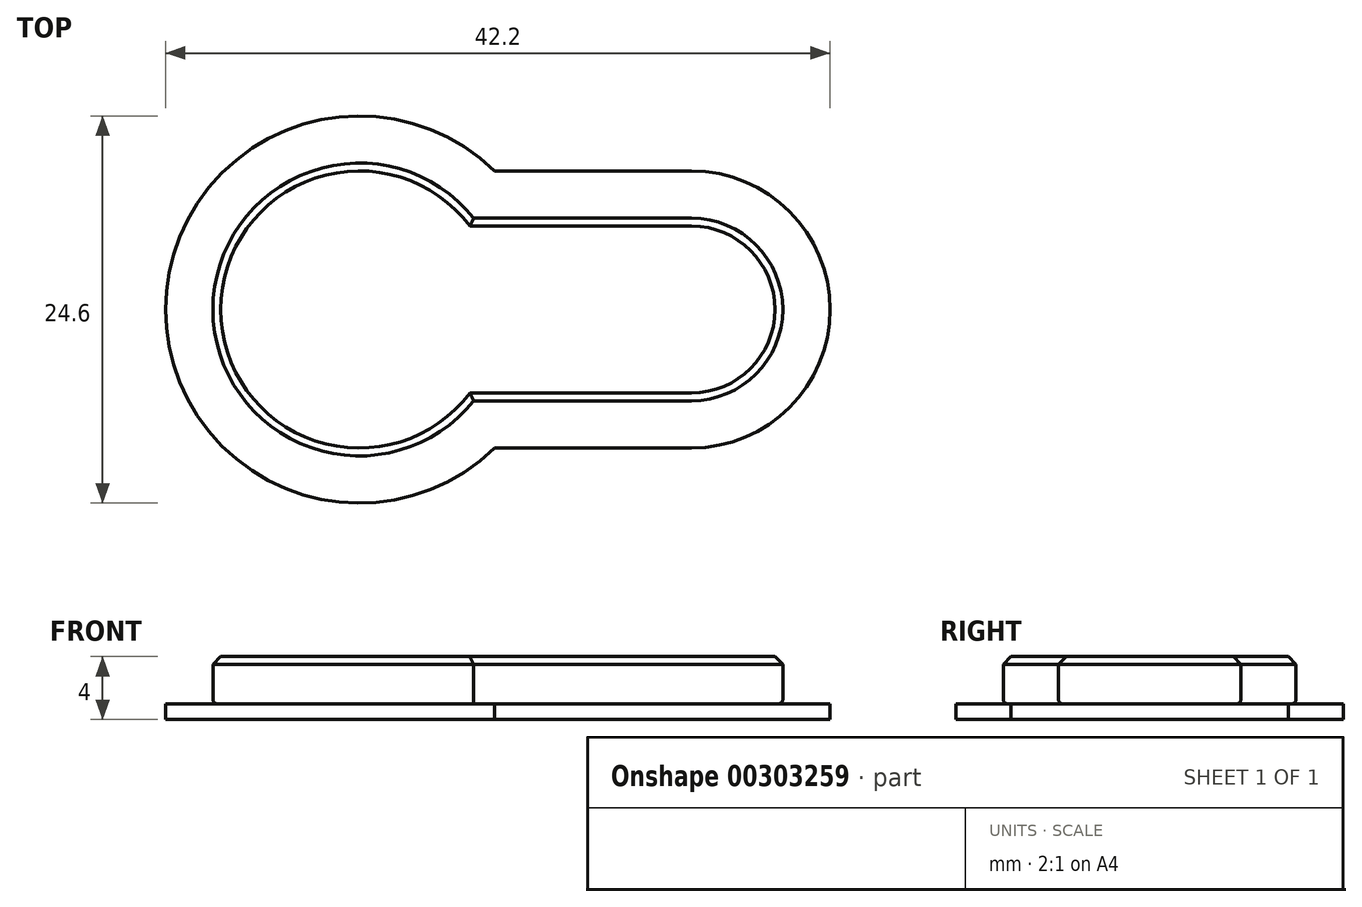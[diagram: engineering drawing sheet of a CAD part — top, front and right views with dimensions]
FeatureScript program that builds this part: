
annotation { "Feature Type Name" : "Feature", "Feature Type Description" : "" }
export const myFeature = defineFeature(function(context is Context, id is Id, definition is map)
    precondition{}
    {
        {
            var Q0;
            Q0=qCreatedBy(makeId("Top.planeOp"),FACE);
            var sketch = newSketch(context, id + "F0", { "sketchPlane" : qUnion([Q0])});
            skArc(sketch, "E0", {"start": v(7.27, 5.8) * mm, "mid": v(-9.3, 0) * mm, "end": v(7.27, -5.8) * mm});
            skArc(sketch, "E1", {"start": v(21.1, -5.8) * mm, "mid": v(26.9, 0) * mm, "end": v(21.1, 5.8) * mm});
            skLineSegment(sketch, "E2", {"start": v(-9.3, 0) * mm, "end": v(-9.3, 19.5) * mm, "construction": true});
            skLineSegment(sketch, "E3", {"start": v(26.9, 0) * mm, "end": v(26.9, 18.68) * mm, "construction": true});
            skLineSegment(sketch, "E4", {"start": v(21.1, -5.8) * mm, "end": v(21.1, 5.8) * mm, "construction": true});
            skLineSegment(sketch, "E5", {"start": v(21.1, 5.8) * mm, "end": v(7.27, 5.8) * mm});
            skLineSegment(sketch, "E6", {"start": v(21.1, -5.8) * mm, "end": v(7.27, -5.8) * mm});
            skSolve(sketch);
        }
        {
            var Q0;
            Q0 = qSketchRegion(id + "F0", true);
            extrude(context, id + "F1", {"entities" : qUnion([Q0]), "depth" : 3 * mm});
        }
        {
            var Q0;
            Q0=makeQuery(id+"F1.opExtrude","CAP_FACE",FACE,{"disambiguationData":[OSD([sQuery(id+"F0.wireOp",EDGE,"E0"),sQuery(id+"F0.wireOp",EDGE,"E1"),sQuery(id+"F0.wireOp",EDGE,"E5"),sQuery(id+"F0.wireOp",EDGE,"E6")])],"isStart":true});
            var sketch = newSketch(context, id + "F2", { "sketchPlane" : qUnion([Q0])});
            skLineSegment(sketch, "E7.0", {"start": v(21.1, -5.8) * mm, "end": v(7.27, -5.8) * mm, "construction": true});
            skArc(sketch, "E7.1", {"start": v(7.27, -5.8) * mm, "mid": v(-9.3, 0) * mm, "end": v(7.27, 5.8) * mm, "construction": true});
            skLineSegment(sketch, "E7.2", {"start": v(21.1, 5.8) * mm, "end": v(7.27, 5.8) * mm, "construction": true});
            skArc(sketch, "E7.3", {"start": v(21.1, 5.8) * mm, "mid": v(26.9, 0) * mm, "end": v(21.1, -5.8) * mm, "construction": true});
            skArc(sketch, "E8.0", {"start": v(21.1, 8.8) * mm, "mid": v(29.9, 0) * mm, "end": v(21.1, -8.8) * mm});
            skLineSegment(sketch, "E8.1", {"start": v(21.1, 8.8) * mm, "end": v(8.6, 8.8) * mm});
            skArc(sketch, "E8.2", {"start": v(8.6, -8.8) * mm, "mid": v(-12.3, 0) * mm, "end": v(8.6, 8.8) * mm});
            skLineSegment(sketch, "E8.3", {"start": v(21.1, -8.8) * mm, "end": v(8.6, -8.8) * mm});
            skSolve(sketch);
        }
        {
            var Q0;
            Q0 = qSketchRegion(id + "F2", true);
            var Q1;
            Q1 = qConstructionFilter(qBodyType(qCreatedBy(id + "F2" ,EDGE), BodyType.WIRE), ConstructionObject.NO);
            extrude(context, id + "F3", {"entities" : qUnion([Q0]), "surfaceEntities" : qUnion([Q1]), "depth" : 1 * mm});
        }
        {
            var Q0;
            Q0=makeQuery(id+"F1.opExtrude","CAP_FACE",FACE,{"disambiguationData":[OSD([sQuery(id+"F0.wireOp",EDGE,"E0"),sQuery(id+"F0.wireOp",EDGE,"E1"),sQuery(id+"F0.wireOp",EDGE,"E5"),sQuery(id+"F0.wireOp",EDGE,"E6")])],"isStart":false});
            chamfer(context, id + "F4", {"entities" : qUnion([Q0]), "width" : 0.5 * mm, "tangentPropagation" : true});
        }
        {
            var Q0;
            Q0=makeQuery(id+"F1.opExtrude","CAP_EDGE",EDGE,{"disambiguationData":[OSD([sQuery(id+"F0.wireOp",EDGE,"E0")])],"isStart":true});
            var Q1;
            Q1=makeQuery(id+"F1.opExtrude","CAP_EDGE",EDGE,{"disambiguationData":[OSD([sQuery(id+"F0.wireOp",EDGE,"E6")])],"isStart":true});
            var Q2;
            Q2=makeQuery(id+"F1.opExtrude","CAP_EDGE",EDGE,{"disambiguationData":[OSD([sQuery(id+"F0.wireOp",EDGE,"E1")])],"isStart":true});
            var Q3;
            Q3=makeQuery(id+"F1.opExtrude","CAP_EDGE",EDGE,{"disambiguationData":[OSD([sQuery(id+"F0.wireOp",EDGE,"E5")])],"isStart":true});
            fillet(context, id + "F5", {"entities" : qUnion([Q0, Q1, Q2, Q3]), "radius" : 0.3 * mm, "tangentPropagation" : true, "allowEdgeOverflow" : false});
        }
    });
